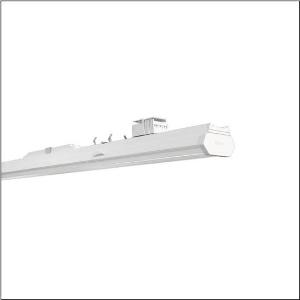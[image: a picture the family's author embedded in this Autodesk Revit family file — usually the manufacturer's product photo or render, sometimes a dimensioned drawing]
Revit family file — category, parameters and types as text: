
# Revit family: licross_r__11_protected_mo_51tp12cn58xf_fcc9
name_source: partatom
category: Lighting Fixtures
units: mm (PartAtom-declared; Revit-internal decimal feet)

## family parameters
Cut with Voids When Loaded = No
Host = Face
Light Source = No
Part Type = Normal
Room Calculation Point = No
Round Connector Dimension = Use Diameter
Shared = No

## types (1)
- --- (1 x LED, 8190 lm, 49 W, 5000K)
    Apparent Load = 49 VA
    CIE Flux Codes = 73 92 98 99 100
    Color Rendering = 80
    Color Temperature = 5000K
    Default Elevation = 1800 mm
    Description = Licross® 11 Protected MO, luminaire insert, of sheet steel, galvanised, coil coated, white, length: 1.500mm, width: 90mm, height: 101mm, LED rated luminous flux: 8.190lm, light colour: 850, control gear: ON/OFF Multilumen, CLOi, control gear: ECG Multilumen, with plug, 3-pole, with phase selection, mains connection: 220..240V, AC, 50/60Hz, start of lifetime: 49W, end of service life: 54W, halogen-free wiring, primary optical cover: cover, of PMMA, light emission: direct distribution, primary light characteristic: symmetric, protection rating (complete): IP64, insulation class (complete): insulation class I (protective earthing), certification: CE, ENEC, VDE, UKCA, protection symbol: D if used in an environment with conductive dust loads with corresponding accessories, impact resistance: IK06, permissible ambient temperature for indoor applications: -35..+40°C, reducing of maximum allowable ambient temperature of 5°C with ceiling mounting, corresponds to IFS (International Featured Standards) requirements for safety and quality in the food industry, LABS conformity tested according to VDMA 24364:2018-05, packaging unit: 1 piece
    Height = 92 mm
    Lamp = 1 x LED
    Lamp Light Flux = 8190 lm
    Lamp Power = 49 W
    Lamp count = 1
    Length = 1500 mm
    Luminous efficacy = 167 lm/W
    Manufacturer = Siteco
    ModVariant = No
    Model = 51TP12CN58XF
    Mounting Place = Ceiling
    Mounting Type = Pendant
    Number of Poles = 1
    OnlyDefault = Yes
    Power Factor = 1
    Product Name = Licross® 11 Protected MO
    Product group = luminaire insert
    ProductGroupID = 901
    Protection Class = Protection class I
    Protection Degree = IP 64
    RLX_Detail_Level = 1
    RLX_Emergency_Light_Flux = 0 lm
    RLX_Emergency_Type = 0
    RLX_Emergency_Type_DB = No
    RlxData = <blob elided: 21997 chars, md5=151ba791>
    Socket = socket
    Standby Power = 0 W
    System Light Flux = 8190 lm
    System Power = 49 W
    Type Comments = factory setting: luminous flux: 100 % | (A | C | E) | 111 mA
    Type Image = l_1256148.jpg
    URL = http://relux.com
    VarID = @adj_143273
    Voltage = 0 V
    Weight = 0.00 kg
    Width = 88 mm

## geometry (parser evidence)
native form markers: Blend x4, Sweep x12
no freeform markers — native parametric forms only
